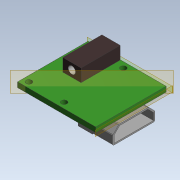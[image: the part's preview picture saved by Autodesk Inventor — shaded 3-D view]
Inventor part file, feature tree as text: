
AUTODESK INVENTOR PART (.ipt)
format: ipt  version: 2020 (Build 240168000, 168)  size: 263,680 bytes
history: native  units: mm
features: extrude x5, sketch x5, projected_geometry x4, plane x3
ambient origin geometry x8: Origin, YZ Plane, XZ Plane, XY Plane, X Axis, Y Axis, Z Axis, Center Point
bodies: Solid1 (feature_tree)
feature tree (17):
  extrude  "Extrusion1"  Depth=27.7mm
  extrude  "Extrusion2"  Depth=21.0mm
  plane  "Work Plane1"
  plane  "Work Plane2"
  plane  "Work Plane3"
  extrude  "Extrusion3"  Depth=2.0mm
  extrude  "Extrusion4"  Depth=6.5mm
  extrude  "Extrusion5"  Depth=4.5mm TaperAngle=0.0deg
  sketch  "Sketch1"  dims[d0=25.0mm d1=27.7mm]
  sketch  "Sketch2"  dims[d2=12.5mm d3=21.0mm]
  projected_geometry  "Projected Loop1"
  sketch  "Sketch4"  dims[d4=2.0mm d5=2.0mm]
  sketch  "Sketch5"  dims[d6=1.8mm d7=0.0mm d8=6.5mm]
  projected_geometry  "Projected Loop3"
  projected_geometry  "Projected Loop4"
  sketch  "Sketch6"  dims[d10=5.0mm d11=4.5mm d12=0.0mm d15=1.0mm d16=1.0mm d17=0.5mm d19=15.0mm d20=5.5mm d21=0.5mm d22=135.0deg d23=3.0mm d24=0.5mm d25=10.5mm d26=0.0mm d27=12.2mm d28=10.5mm d29=0.0mm d30=2.6mm d31=10.0mm d32=0.0mm d33=14.0mm d34=0.1mm]
  projected_geometry  "Projected Loop5"
